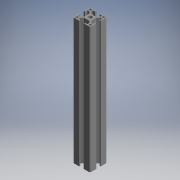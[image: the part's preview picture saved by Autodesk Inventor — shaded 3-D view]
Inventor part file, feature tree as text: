
AUTODESK INVENTOR PART (.ipt)
format: ipt  version: 2017.3 (Build 213256000, 256)  size: 210,432 bytes
history: native  units: mm (DEFAULTED — no unit token found)
features: other x21, sketch x3, hole x2, extrude x1, pattern_linear x1
ambient origin geometry x8: Origin, YZ Plane, XZ Plane, XY Plane, X Axis, Y Axis, Z Axis, Center Point
bodies: Solid1 (feature_tree)
feature tree (28):
  extrude  "Extrusion1"  Depth=223.0mm
  hole  "Hole1"  [1 undecoded]
  hole  "Hole2"  [1 undecoded]
  pattern_linear  "Rectangular Pattern1"  [2 undecoded]
  other  "C1_XY"
  other  "C1_YZ"
  other  "C1_ZX"
  other  "C1_X"
  other  "C1_Y"
  other  "C1_Z"
  other  "C1_Center"
  other  "to_frame_cap1_XY"
  other  "to_frame_cap1_YZ"
  other  "to_frame_cap1_ZX"
  other  "to_frame_cap1_X"
  other  "to_frame_cap1_Y"
  other  "to_frame_cap1_Z"
  other  "to_frame_cap1_Center"
  other  "to_frame_cap2_XY"
  other  "to_frame_cap2_YZ"
  other  "to_frame_cap2_ZX"
  other  "to_frame_cap2_X"
  other  "to_frame_cap2_Y"
  other  "to_frame_cap2_Z"
  other  "to_frame_cap2_Center"
  sketch  "Sketch_1"  dims[d0=223.0mm d1=0.0mm]
  sketch  "Sketch2"  dims[d2=6.8mm d3=6.0mm d4=4.0mm d5=2.0mm d6=90.0deg d7=223.0mm d8=0.0mm]
  sketch  "Sketch3"  dims[d9=4.2mm d10=6.0mm d11=4.0mm d12=2.0mm d13=90.0deg d14=223.0mm d15=0.0mm d16=20.0mm d18=23.2mm d19=20.0mm d21=23.2mm d22=0.0mm d23=0.0mm d24=0.0mm]
note: 4 required parameter values undecoded (feature->parameter linkage not recoverable at this tier; creation-order binding heuristic only, values carry confidence <= 0.55)
